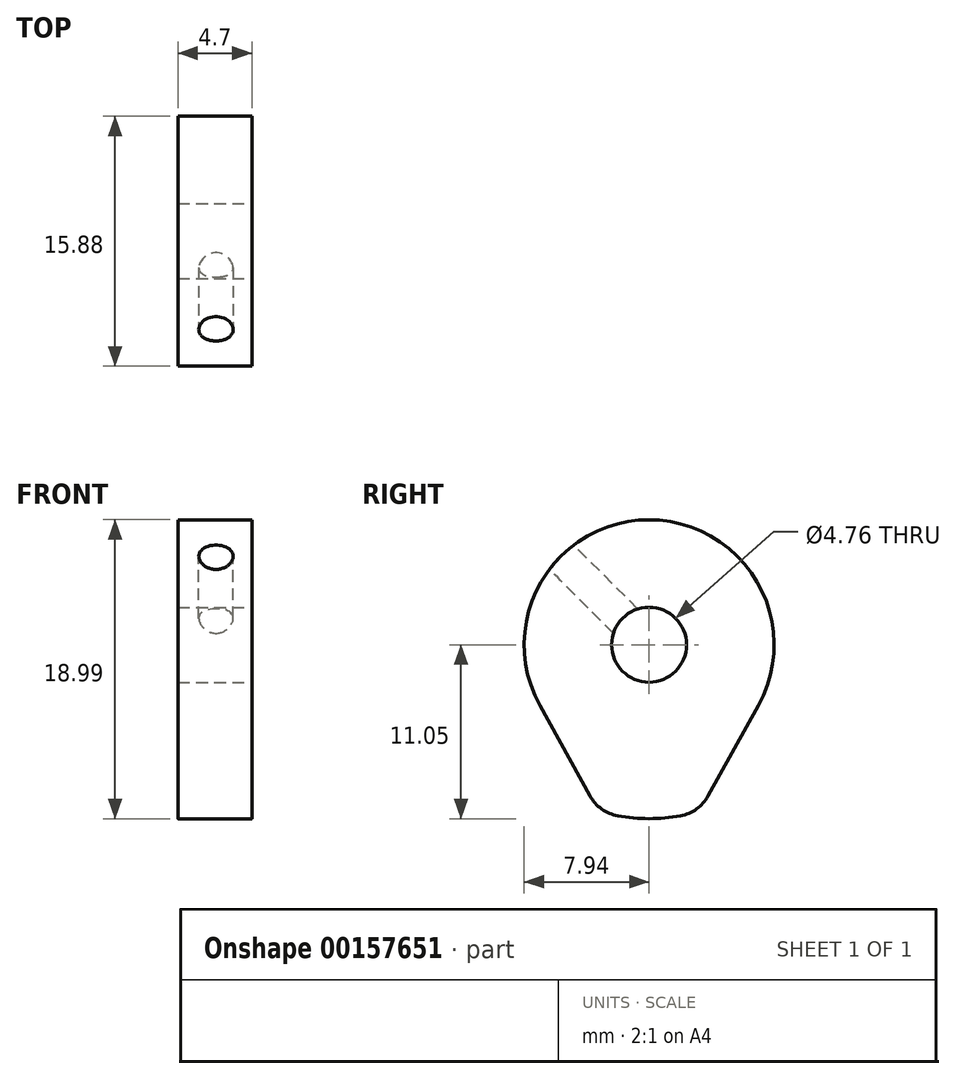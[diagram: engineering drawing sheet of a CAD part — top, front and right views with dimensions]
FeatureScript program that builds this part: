
annotation { "Feature Type Name" : "Feature", "Feature Type Description" : "" }
export const myFeature = defineFeature(function(context is Context, id is Id, definition is map)
    precondition{}
    {
        {
            var Q0;
            Q0=qCreatedBy(makeId("Right.planeOp"),FACE);
            var sketch = newSketch(context, id + "F0", { "sketchPlane" : qUnion([Q0])});
            skArc(sketch, "E0", {"start": v(-1.99, -10.87) * mm, "mid": v(0, -11.05) * mm, "end": v(1.99, -10.87) * mm});
            skArc(sketch, "E1", {"start": v(6.94, -3.85) * mm, "mid": v(6.84, 4.03) * mm, "end": v(0, 7.94) * mm});
            skLineSegment(sketch, "E2", {"start": v(0, 0) * mm, "end": v(0, -22.05) * mm, "construction": true});
            skLineSegment(sketch, "E3", {"start": v(-6.94, -3.85) * mm, "end": v(-3.75, -9.6) * mm});
            skLineSegment(sketch, "E4", {"start": v(6.94, -3.85) * mm, "end": v(3.75, -9.6) * mm});
            skArc(sketch, "E5.filletArc", {"start": v(-3.75, -9.6) * mm, "mid": v(-3.01, -10.43) * mm, "end": v(-1.99, -10.87) * mm});
            skArc(sketch, "E6.filletArc", {"start": v(1.99, -10.87) * mm, "mid": v(3.01, -10.43) * mm, "end": v(3.75, -9.6) * mm});
            skCircle(sketch, "E7", {"center": v(0, 0) * mm, "radius": 2.38 * mm});
            skPoint(sketch, "E8.start.orphan", {"position": v(0, 7.94) * mm});
            skLineSegment(sketch, "E9", {"start": v(0, 7.94) * mm, "end": v(0, 7.94) * mm});
            skLineSegment(sketch, "E10", {"start": v(-6.94, -3.85) * mm, "end": v(-6.94, -3.85) * mm});
            skPoint(sketch, "E11.visualSharp", {"position": v(-13.48, 7.94) * mm});
            skArc(sketch, "E11.filletArc", {"start": v(0, 7.94) * mm, "mid": v(-6.84, 4.03) * mm, "end": v(-6.94, -3.85) * mm});
            skLineSegment(sketch, "E12", {"start": v(0, 0) * mm, "end": v(-5.61, 5.61) * mm, "construction": true});
            skLineSegment(sketch, "E13", {"start": v(0, 0) * mm, "end": v(5.61, 5.61) * mm, "construction": true});
            skSolve(sketch);
        }
        {
            var Q0;
            Q0=makeQuery(id+"F0.imprint","IMPRINT",FACE,{"disambiguationData":[TD([[makeQuery(id+"F0.imprint","IMPRINT",EDGE,{"derivedFrom":sQuery(id+"F0.wireOp",EDGE,"E0")}),1.0]])]});
            extrude(context, id + "F1", {"entities" : qUnion([Q0]), "oppositeDirection" : true, "depth" : 4.7 * mm});
        }
        {
            var Q0;
            Q0=sQuery(id+"F0.wireOp",EDGE,"E12");
            var Q1;
            Q1=sQuery(id+"F0.wireOp",VERTEX,"E12.end");
            cPlane(context, id + "F2", {"entities" : qUnion([Q0, Q1]), "cplaneType" : CPlaneType.LINE_POINT, "offset" : 25.4 * mm, "width" : 152.4 * mm, "height" : 152.4 * mm});
        }
        {
            var Q0;
            Q0=qCreatedBy(id+"F2.planeOp",FACE);
            var sketch = newSketch(context, id + "F3", { "sketchPlane" : qUnion([Q0])});
            skCircle(sketch, "E14", {"center": v(-2.29, 0) * mm, "radius": 1.1 * mm});
            skSolve(sketch);
        }
        {
            var Q0;
            Q0=makeQuery(id+"F3.imprint","IMPRINT",FACE,{"disambiguationData":[TD([[makeQuery(id+"F3.imprint","IMPRINT",EDGE,{"derivedFrom":sQuery(id+"F3.wireOp",EDGE,"E14")}),1.0]])]});
            extrude(context, id + "F4", {"entities" : qUnion([Q0]), "operationType" : NewBodyOperationType.REMOVE, "oppositeDirection" : true, "depth" : 7.62 * mm});
        }
        {
            var Q0;
            Q0=sQuery(id+"F0.wireOp",EDGE,"E13");
            var Q1;
            Q1=sQuery(id+"F0.wireOp",VERTEX,"E13.end");
            cPlane(context, id + "F5", {"entities" : qUnion([Q0, Q1]), "cplaneType" : CPlaneType.LINE_POINT, "offset" : 25.4 * mm, "width" : 152.4 * mm, "height" : 152.4 * mm});
        }
        {
            var Q0;
            Q0=qCreatedBy(id+"F5.planeOp",FACE);
            var sketch = newSketch(context, id + "F6", { "sketchPlane" : qUnion([Q0])});
            skCircle(sketch, "E15", {"center": v(-2.29, 0) * mm, "radius": 1.1 * mm});
            skSolve(sketch);
        }
        {
            var Q0;
            Q0=makeQuery(id+"F6.imprint","IMPRINT",FACE,{"disambiguationData":[TD([[makeQuery(id+"F6.imprint","IMPRINT",EDGE,{"derivedFrom":sQuery(id+"F6.wireOp",EDGE,"E15")}),1.0]])]});
            extrude(context, id + "F7", {"entities" : qUnion([Q0]), "operationType" : NewBodyOperationType.REMOVE, "oppositeDirection" : true, "depth" : 7.62 * mm});
        }
    });
